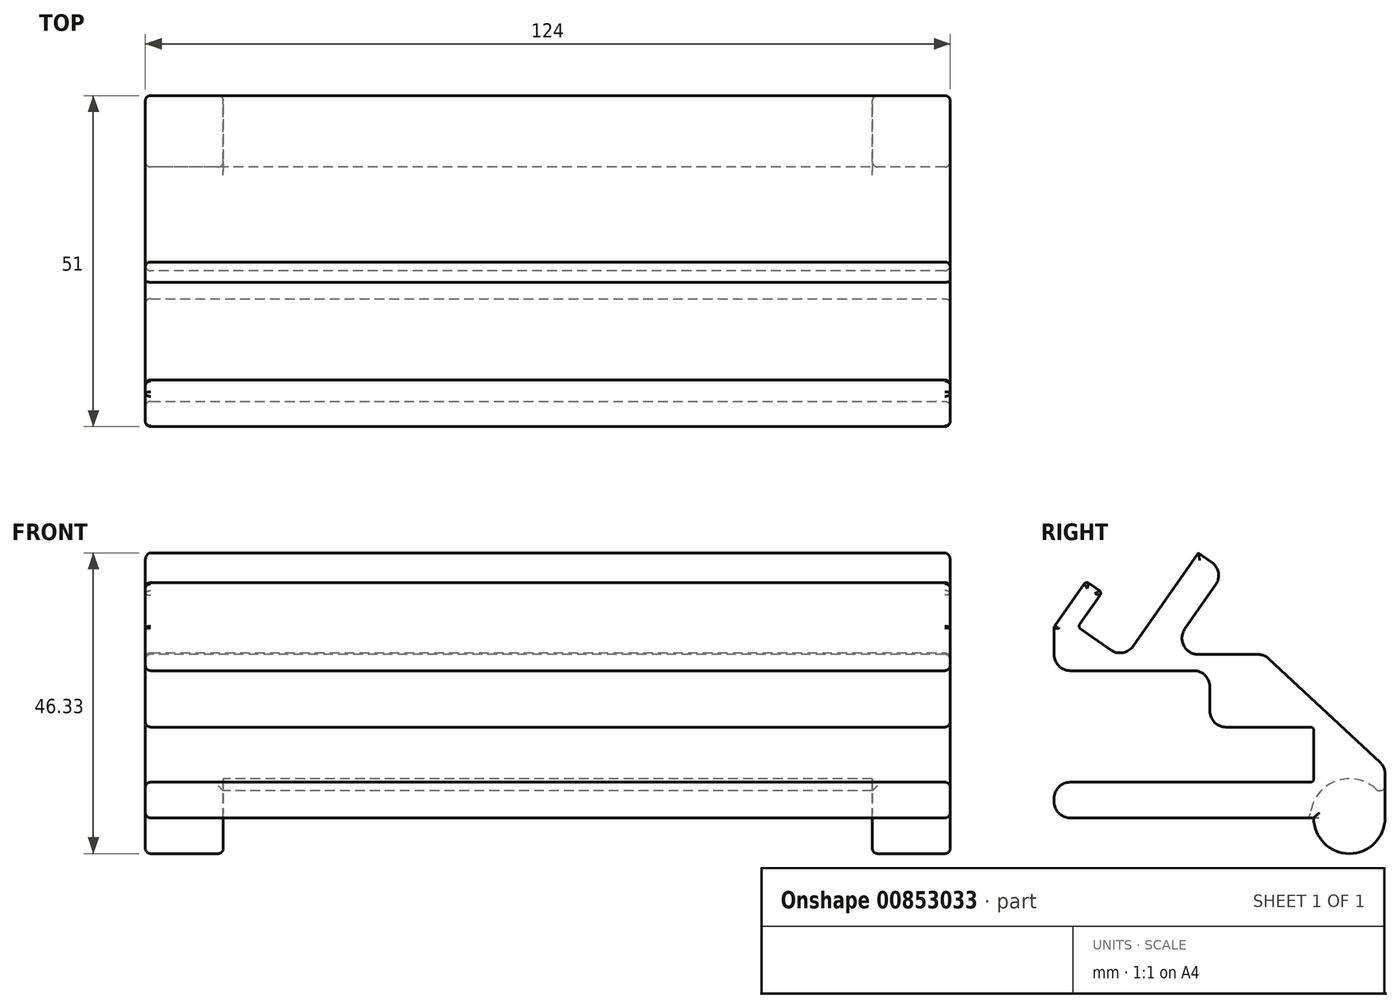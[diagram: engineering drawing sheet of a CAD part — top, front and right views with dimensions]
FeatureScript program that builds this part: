
annotation { "Feature Type Name" : "Feature", "Feature Type Description" : "" }
export const myFeature = defineFeature(function(context is Context, id is Id, definition is map)
    precondition{}
    {
        {
            var Q0;
            Q0=qCreatedBy(makeId("Right.planeOp"),FACE);
            var sketch = newSketch(context, id + "F0", { "sketchPlane" : qUnion([Q0])});
            skLineSegment(sketch, "E0", {"start": v(-5.5, 5.5) * mm, "end": v(-5.5, 14) * mm});
            skLineSegment(sketch, "E1", {"start": v(-21.5, 22.7) * mm, "end": v(-45.5, 22.7) * mm});
            skLineSegment(sketch, "E2", {"start": v(-45.5, 29.43) * mm, "end": v(-40.57, 36.47) * mm});
            skLineSegment(sketch, "E3", {"start": v(-45.5, 0) * mm, "end": v(-45.5, 5.5) * mm});
            skLineSegment(sketch, "E4", {"start": v(-40.57, 36.47) * mm, "end": v(-38.1, 34.75) * mm});
            skLineSegment(sketch, "E5", {"start": v(-38.1, 34.75) * mm, "end": v(-41.84, 29.43) * mm});
            skLineSegment(sketch, "E6", {"start": v(-41.84, 29.43) * mm, "end": v(-34.73, 24.45) * mm});
            skLineSegment(sketch, "E7", {"start": v(-34.73, 24.45) * mm, "end": v(-23.26, 40.83) * mm});
            skLineSegment(sketch, "E8", {"start": v(-45.5, 29.43) * mm, "end": v(-45.5, 22.7) * mm});
            skArc(sketch, "E9", {"start": v(-5.5, 0) * mm, "mid": v(0, -5.5) * mm, "end": v(5.5, 0) * mm});
            skLineSegment(sketch, "E10", {"start": v(-5.5, 0) * mm, "end": v(-45.5, 0) * mm});
            skLineSegment(sketch, "E11", {"start": v(5.5, 0) * mm, "end": v(5.5, 7.85) * mm});
            skLineSegment(sketch, "E12", {"start": v(-5.5, 5.5) * mm, "end": v(-45.5, 5.5) * mm});
            skLineSegment(sketch, "E13", {"start": v(-5.5, 14) * mm, "end": v(-21.5, 14) * mm});
            skLineSegment(sketch, "E14", {"start": v(0, 0) * mm, "end": v(36.24, 51.75) * mm, "construction": true});
            skLineSegment(sketch, "E15", {"start": v(0, 0) * mm, "end": v(57.48, 0) * mm, "construction": true});
            skLineSegment(sketch, "E16", {"start": v(-21.5, 22.7) * mm, "end": v(-21.5, 14) * mm});
            skLineSegment(sketch, "E17", {"start": v(-23.26, 40.83) * mm, "end": v(-19.16, 37.97) * mm});
            skLineSegment(sketch, "E18", {"start": v(-19.16, 37.97) * mm, "end": v(-28.1, 25.2) * mm});
            skLineSegment(sketch, "E19", {"start": v(-28.1, 25.2) * mm, "end": v(-13.12, 25.2) * mm});
            skLineSegment(sketch, "E20", {"start": v(-13.12, 25.2) * mm, "end": v(5.5, 7.85) * mm});
            skSolve(sketch);
        }
        {
            var Q0;
            Q0=makeQuery(id+"F0.imprint","IMPRINT",FACE,{"disambiguationData":[TD([[makeQuery(id+"F0.imprint","IMPRINT",EDGE,{"derivedFrom":sQuery(id+"F0.wireOp",EDGE,"QAfU7S68-Y1Ye-0Cms-aJwV-xw8ddjo1FXWS")}),-1.0]])]});
            var Q1;
            Q1=makeQuery(id+"F0.imprint","IMPRINT",FACE,{"disambiguationData":[TD([[makeQuery(id+"F0.imprint","IMPRINT",EDGE,{"derivedFrom":sQuery(id+"F0.wireOp",EDGE,"E0")}),-1.0]])]});
            extrude(context, id + "F1", {"entities" : qUnion([Q0, Q1]), "depth" : (114 + 10) * mm, "offsetDistance" : 25 * mm, "symmetric" : true});
        }
        {
            var Q0;
            Q0=qCreatedBy(makeId("Right.planeOp"),FACE);
            var sketch = newSketch(context, id + "F2", { "sketchPlane" : qUnion([Q0])});
            skCircle(sketch, "E21", {"center": v(0, 0) * mm, "radius": 6.04 * mm});
            skSolve(sketch);
        }
        {
            var Q0;
            Q0 = qSketchRegion(id + "F2", true);
            var Q1;
            Q1=sQuery(id+"F2.wireOp",EDGE,"E21");
            extrude(context, id + "F3", {"entities" : qUnion([Q0]), "operationType" : NewBodyOperationType.REMOVE, "surfaceEntities" : qUnion([Q1]), "depth" : 100 * mm, "offsetDistance" : 25 * mm, "symmetric" : true});
        }
        {
            var Q0;
            Q0=makeQuery(id+"F1.opExtrude","SWEPT_EDGE",EDGE,{"disambiguationData":[OSD([sQuery(id+"F0.wireOp",EDGE,"E11"),sQuery(id+"F0.wireOp",EDGE,"2Ov2tPmu-FMbM-GlEZ-FjO8-IeoaFAeKC6pt")])]});
            var Q1;
            Q1=makeQuery(id+"F1.opExtrude","SWEPT_EDGE",EDGE,{"disambiguationData":[OSD([sQuery(id+"F0.wireOp",EDGE,"E17"),sQuery(id+"F0.wireOp",EDGE,"E18")])]});
            var Q2;
            Q2=makeQuery(id+"F1.opExtrude","SWEPT_EDGE",EDGE,{"disambiguationData":[OSD([sQuery(id+"F0.wireOp",EDGE,"E18"),sQuery(id+"F0.wireOp",EDGE,"2Ov2tPmu-FMbM-GlEZ-FjO8-IeoaFAeKC6pt")])]});
            var Q3;
            Q3=makeQuery(id+"F1.opExtrude","SWEPT_EDGE",EDGE,{"disambiguationData":[OSD([sQuery(id+"F0.wireOp",EDGE,"E1"),sQuery(id+"F0.wireOp",EDGE,"E16")])]});
            var Q4;
            Q4=makeQuery(id+"F1.opExtrude","SWEPT_EDGE",EDGE,{"disambiguationData":[OSD([sQuery(id+"F0.wireOp",EDGE,"E13"),sQuery(id+"F0.wireOp",EDGE,"E16")])]});
            var Q5;
            Q5=makeQuery(id+"F1.opExtrude","SWEPT_EDGE",EDGE,{"disambiguationData":[OSD([sQuery(id+"F0.wireOp",EDGE,"E3"),sQuery(id+"F0.wireOp",EDGE,"E10")])]});
            var Q6;
            Q6=makeQuery(id+"F1.opExtrude","SWEPT_EDGE",EDGE,{"disambiguationData":[OSD([sQuery(id+"F0.wireOp",EDGE,"E6"),sQuery(id+"F0.wireOp",EDGE,"E7")])]});
            var Q7;
            Q7=makeQuery(id+"F1.opExtrude","SWEPT_EDGE",EDGE,{"disambiguationData":[OSD([sQuery(id+"F0.wireOp",EDGE,"E19"),sQuery(id+"F0.wireOp",EDGE,"E20")])]});
            var Q8;
            Q8=makeQuery(id+"F1.opExtrude","SWEPT_EDGE",EDGE,{"disambiguationData":[OSD([sQuery(id+"F0.wireOp",EDGE,"E1"),sQuery(id+"F0.wireOp",EDGE,"E8")])]});
            var Q9;
            Q9=makeQuery(id+"F1.opExtrude","SWEPT_EDGE",EDGE,{"disambiguationData":[OSD([sQuery(id+"F0.wireOp",EDGE,"E3"),sQuery(id+"F0.wireOp",EDGE,"E12")])]});
            fillet(context, id + "F4", {"entities" : qUnion([Q0, Q1, Q2, Q3, Q4, Q5, Q6, Q7, Q8, Q9]), "radius" : 2.5 * mm, "tangentPropagation" : true, "allowEdgeOverflow" : false});
        }
        {
            var Q0;
            Q0=makeQuery(id+"F1.opExtrude","SWEPT_EDGE",EDGE,{"disambiguationData":[OSD([sQuery(id+"F0.wireOp",EDGE,"E2"),sQuery(id+"F0.wireOp",EDGE,"E8")])]});
            var Q1;
            Q1=makeQuery(id+"F1.opExtrude","SWEPT_EDGE",EDGE,{"disambiguationData":[OSD([sQuery(id+"F0.wireOp",EDGE,"E2"),sQuery(id+"F0.wireOp",EDGE,"E4")])]});
            var Q2;
            Q2=makeQuery(id+"F1.opExtrude","SWEPT_EDGE",EDGE,{"disambiguationData":[OSD([sQuery(id+"F0.wireOp",EDGE,"E5"),sQuery(id+"F0.wireOp",EDGE,"E6")])]});
            var Q3;
            Q3=makeQuery(id+"F1.opExtrude","SWEPT_EDGE",EDGE,{"disambiguationData":[OSD([sQuery(id+"F0.wireOp",EDGE,"E4"),sQuery(id+"F0.wireOp",EDGE,"E5")])]});
            var Q4;
            Q4=makeQuery(id+"F1.opExtrude","SWEPT_EDGE",EDGE,{"disambiguationData":[OSD([sQuery(id+"F0.wireOp",EDGE,"E0"),sQuery(id+"F0.wireOp",EDGE,"E12")])]});
            var Q5;
            Q5=makeQuery(id+"F1.opExtrude","SWEPT_EDGE",EDGE,{"disambiguationData":[OSD([sQuery(id+"F0.wireOp",EDGE,"E0"),sQuery(id+"F0.wireOp",EDGE,"E13")])]});
            fillet(context, id + "F5", {"entities" : qUnion([Q0, Q1, Q2, Q3, Q4, Q5]), "radius" : .5 * mm, "tangentPropagation" : true, "allowEdgeOverflow" : false});
        }
        {
            var Q0;
            Q0=makeQuery(id+"F1.opExtrude","CAP_FACE",FACE,{"disambiguationData":[OSD([sQuery(id+"F0.wireOp",EDGE,"E0"),sQuery(id+"F0.wireOp",EDGE,"E1"),sQuery(id+"F0.wireOp",EDGE,"E2"),sQuery(id+"F0.wireOp",EDGE,"E3"),sQuery(id+"F0.wireOp",EDGE,"E4"),sQuery(id+"F0.wireOp",EDGE,"E5"),sQuery(id+"F0.wireOp",EDGE,"E6"),sQuery(id+"F0.wireOp",EDGE,"E7"),sQuery(id+"F0.wireOp",EDGE,"LO4chNdI-tx0R-I1rq-ZKnn-9fisZVerJWpT"),sQuery(id+"F0.wireOp",EDGE,"E8"),sQuery(id+"F0.wireOp",EDGE,"E9"),sQuery(id+"F0.wireOp",EDGE,"E10"),sQuery(id+"F0.wireOp",EDGE,"E11"),sQuery(id+"F0.wireOp",EDGE,"E12"),sQuery(id+"F0.wireOp",EDGE,"E13"),sQuery(id+"F0.wireOp",EDGE,"E16")])],"isStart":false});
            var Q1;
            Q1=makeQuery(id+"F1.opExtrude","CAP_FACE",FACE,{"disambiguationData":[OSD([sQuery(id+"F0.wireOp",EDGE,"E0"),sQuery(id+"F0.wireOp",EDGE,"E1"),sQuery(id+"F0.wireOp",EDGE,"E2"),sQuery(id+"F0.wireOp",EDGE,"E3"),sQuery(id+"F0.wireOp",EDGE,"E4"),sQuery(id+"F0.wireOp",EDGE,"E5"),sQuery(id+"F0.wireOp",EDGE,"E6"),sQuery(id+"F0.wireOp",EDGE,"E7"),sQuery(id+"F0.wireOp",EDGE,"LO4chNdI-tx0R-I1rq-ZKnn-9fisZVerJWpT"),sQuery(id+"F0.wireOp",EDGE,"E8"),sQuery(id+"F0.wireOp",EDGE,"E9"),sQuery(id+"F0.wireOp",EDGE,"E10"),sQuery(id+"F0.wireOp",EDGE,"E11"),sQuery(id+"F0.wireOp",EDGE,"E12"),sQuery(id+"F0.wireOp",EDGE,"E13"),sQuery(id+"F0.wireOp",EDGE,"E16")])],"isStart":true});
            var Q2;
            Q2=makeQuery(id+"F3.boolean.opBoolean","INTERSECT",EDGE,{"derivedFrom":[makeQuery(id+"F1.opExtrude","SWEPT_FACE",FACE,{"disambiguationData":[OSD([sQuery(id+"F0.wireOp",EDGE,"E10")])]}),makeQuery(id+"F3.opExtrude","SWEPT_FACE",FACE,{"disambiguationData":[OSD([sQuery(id+"F2.wireOp",EDGE,"E21")])]})]});
            var Q3;
            Q3=makeQuery(id+"F3.boolean.opBoolean","INTERSECT",EDGE,{"derivedFrom":[makeQuery(id+"F1.opExtrude","SWEPT_FACE",FACE,{"disambiguationData":[OSD([sQuery(id+"F0.wireOp",EDGE,"E11")])]}),makeQuery(id+"F3.opExtrude","SWEPT_FACE",FACE,{"disambiguationData":[OSD([sQuery(id+"F2.wireOp",EDGE,"E21")])]})]});
            var Q4;
            Q4=makeQuery(id+"F3.boolean.opBoolean","INTERSECT",EDGE,{"derivedFrom":[makeQuery(id+"F1.opExtrude","SWEPT_FACE",FACE,{"disambiguationData":[OSD([sQuery(id+"F0.wireOp",EDGE,"E9")])]}),makeQuery(id+"F3.opExtrude","CAP_FACE",FACE,{"disambiguationData":[OSD([sQuery(id+"F2.wireOp",EDGE,"E21")])],"isStart":false})]});
            var Q5;
            Q5=makeQuery(id+"F3.boolean.opBoolean","INTERSECT",EDGE,{"derivedFrom":[makeQuery(id+"F1.opExtrude","SWEPT_FACE",FACE,{"disambiguationData":[OSD([sQuery(id+"F0.wireOp",EDGE,"E9")])]}),makeQuery(id+"F3.opExtrude","CAP_FACE",FACE,{"disambiguationData":[OSD([sQuery(id+"F2.wireOp",EDGE,"E21")])],"isStart":true})]});
            fillet(context, id + "F6", {"entities" : qUnion([Q0, Q1, Q2, Q3, Q4, Q5]), "radius" : .8 * mm, "tangentPropagation" : true, "allowEdgeOverflow" : false});
        }
    });
